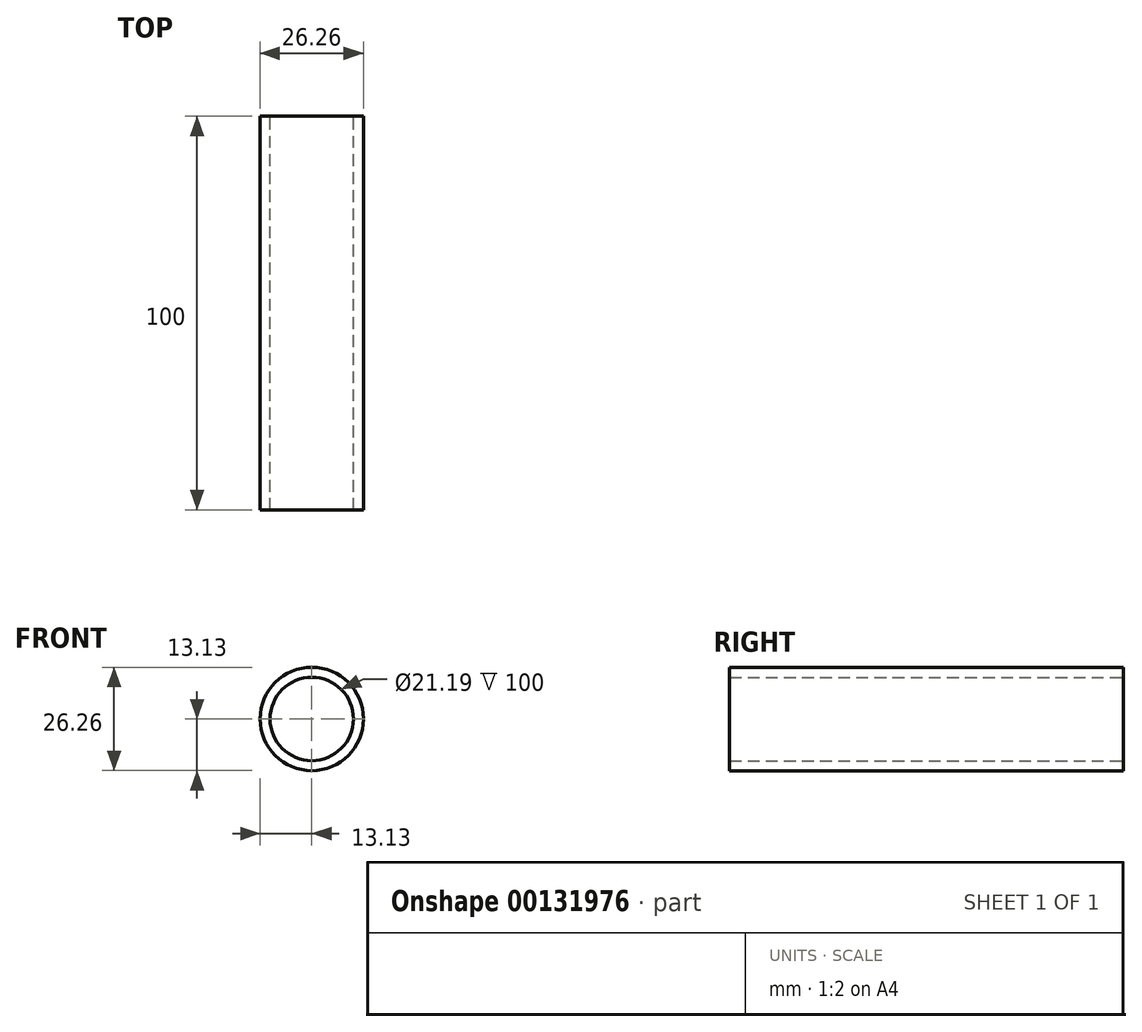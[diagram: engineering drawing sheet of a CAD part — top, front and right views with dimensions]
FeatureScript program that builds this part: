
annotation { "Feature Type Name" : "Feature", "Feature Type Description" : "" }
export const myFeature = defineFeature(function(context is Context, id is Id, definition is map)
    precondition{}
    {
        {
            var Q0;
            Q0=qCreatedBy(makeId("Front.planeOp"),FACE);
            var sketch = newSketch(context, id + "F0", { "sketchPlane" : qUnion([Q0])});
            skCircle(sketch, "E0", {"center": v(0, 0) * mm, "radius": 13.13 * mm});
            skCircle(sketch, "E1", {"center": v(0, 0) * mm, "radius": 10.6 * mm});
            skSolve(sketch);
        }
        {
            var Q0;
            Q0=makeQuery(id+"F0.imprint","IMPRINT",FACE,{"disambiguationData":[TD([[makeQuery(id+"F0.imprint","IMPRINT",EDGE,{"derivedFrom":sQuery(id+"F0.wireOp",EDGE,"E0")}),1.0]])]});
            var Q1;
            Q1=sQuery(id+"F0.wireOp",EDGE,"E0");
            var Q2;
            Q2=sQuery(id+"F0.wireOp",EDGE,"E1");
            extrude(context, id + "F1", {"entities" : qUnion([Q0]), "surfaceEntities" : qUnion([Q1, Q2]), "depth" : 100 * mm});
        }
    });
